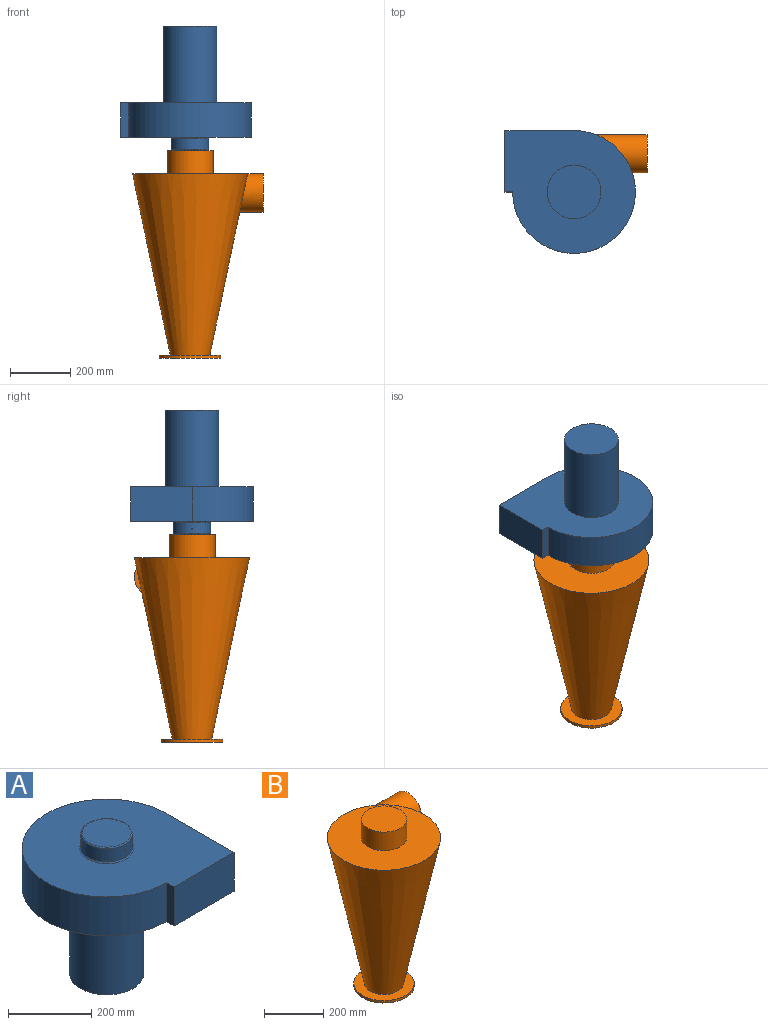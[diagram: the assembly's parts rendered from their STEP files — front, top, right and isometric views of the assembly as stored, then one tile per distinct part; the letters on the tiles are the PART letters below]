
ASSEMBLY  parts=2 mates=1
PART A: 14 faces, bbox 406.4x431.8x412.8 mm
  f0: torus R=58.74mm, axis (0,0,1), area 1903.9mm2, adj f1,f2
  f1: cylinder r=61.91mm len=123.83mm, axis (0,0,1), area 14807mm2, adj f0,f3,f6
  f2: plane 117.48x117.48mm, normal (0,0,1), area 10838.8mm2, adj f0
  f3: torus R=65.09mm, axis (0,0,1), area 1976.2mm2, adj f1,f4
  f4: plane 431.8x406.4mm, normal (0,0,1), area 130430.4mm2, adj f3,f9,f10,f11,f12
  f5: plane 4.23x4.23mm, normal (0,-1,0), area 14.1mm2, adj f6
  f6: cylinder r=2.12mm len=61.88mm, axis (0,-1,0), area 822.9mm2, adj f1,f5
  f7: cylinder r=88.9mm len=254mm, axis (0,0,-1), area 141878.1mm2, adj f8,f13
  f8: plane 431.8x406.4mm, normal (0,0,-1), area 118910.7mm2, adj f7,f9,f10,f11,f12
  f9: plane 114.3x25.4mm, normal (-1,0,0), area 2903.2mm2, adj f4,f8,f10,f12
  f10: plane 203.2x114.3mm, normal (0,-1,0), area 23225.8mm2, adj f4,f8,f9,f11
  f11: plane 228.6x114.3mm, normal (1,0,0), area 26129mm2, adj f4,f8,f10,f12
  f12: cylinder r=203.2mm len=406.4mm, axis (0,0,-1), area 109448.8mm2, adj f4,f8,f9,f11
  f13: plane 177.8x177.8mm, normal (0,0,-1), area 24828.7mm2, adj f7
PART B: 10 faces, bbox 431.8x381x685.8 mm
  f0: cone r=190.5mm half-angle=11.8deg, axis (0,0,1), area 470817.8mm2, adj f3,f4,f5,f8
  f1: cylinder r=76.2mm len=152.4mm, axis (0,0,-1), area 36482.9mm2, adj f2,f3
  f2: plane 152.4x152.4mm, normal (0,0,1), area 18241.5mm2, adj f1
  f3: plane 381x381mm, normal (0,0,1), area 95767.7mm2, adj f0,f1
  f4: cylinder r=63.5mm len=241.3mm, axis (-1,0,0), area 56345.1mm2, adj f0,f5,f6
  f5: plane 78.57x23.5mm, normal (-1,0,0), area 783.4mm2, adj f0,f4
  f6: plane 127x127mm, normal (1,0,0), area 12667.7mm2, adj f4
  f7: cylinder r=101.6mm len=203.2mm, axis (0,0,-1), area 6080.5mm2, adj f8,f9
  f8: plane 203.2x203.2mm, normal (0,0,1), area 18957.5mm2, adj f0,f7
  f9: plane 203.2x203.2mm, normal (0,0,-1), area 32429.3mm2, adj f7
PLACE A rot(axis=(-0.71,-0.71,0),180deg) t=(0,-609.6,736.79)mm
PLACE B t=(0,0,609.6)mm
MATE fastened A.f0 <-> B.f1  axis (0,0,-1) through (0,0,685.8)mm
